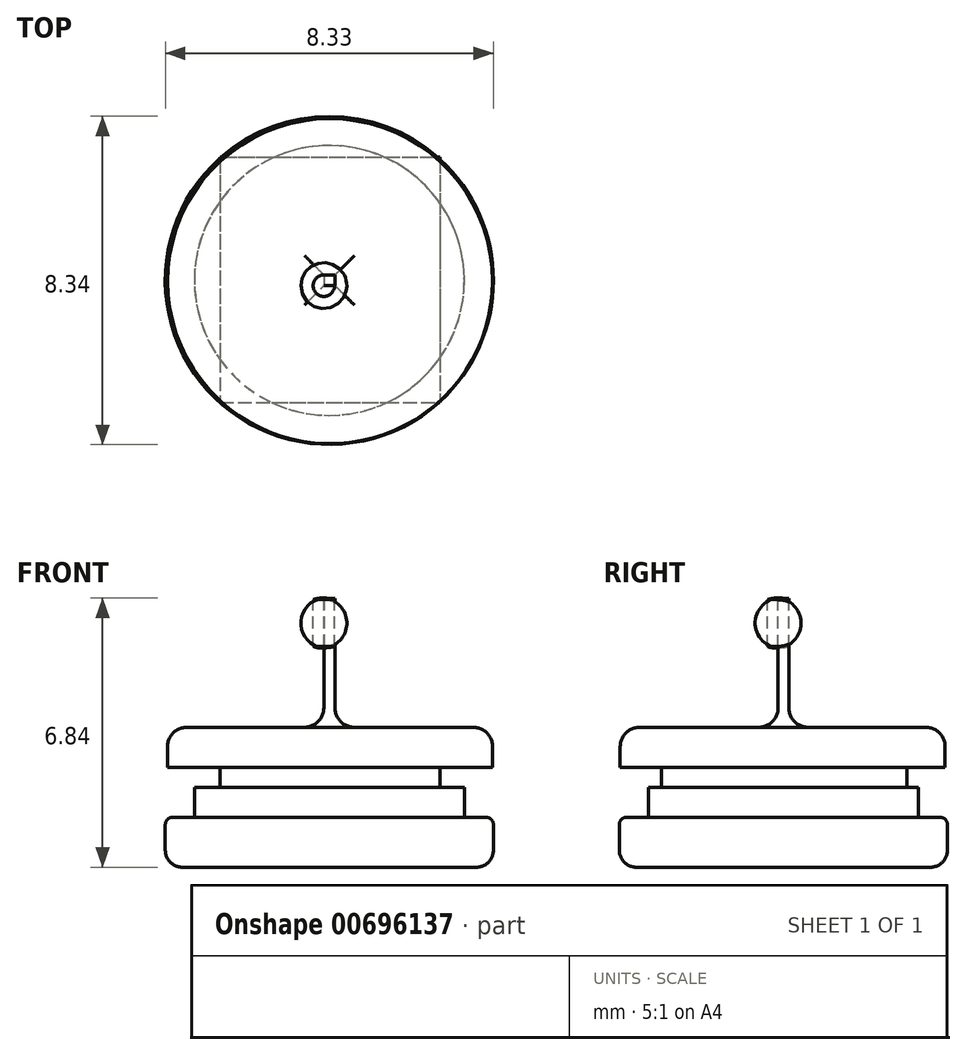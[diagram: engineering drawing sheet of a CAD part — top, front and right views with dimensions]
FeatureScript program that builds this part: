
annotation { "Feature Type Name" : "Feature", "Feature Type Description" : "" }
export const myFeature = defineFeature(function(context is Context, id is Id, definition is map)
    precondition{}
    {
        {
            var Q0;
            Q0=qCreatedBy(makeId("Top.planeOp"),FACE);
            var sketch = newSketch(context, id + "F0", { "sketchPlane" : qUnion([Q0])});
            skCircle(sketch, "E0", {"center": v(-38.02, 10.25) * mm, "radius": 4.17 * mm});
            skSolve(sketch);
        }
        {
            var Q0;
            Q0=makeQuery(id+"F0.imprint","IMPRINT",FACE,{"disambiguationData":[TD([[makeQuery(id+"F0.imprint","IMPRINT",EDGE,{"derivedFrom":sQuery(id+"F0.wireOp",EDGE,"E0")}),1.0]])]});
            var sketch = newSketch(context, id + "F1", { "sketchPlane" : qUnion([Q0])});
            skSolve(sketch);
        }
        {
            var Q0;
            Q0 = qSketchRegion(id + "F1", true);
            var Q1;
            Q1=makeQuery(id+"F0.imprint","IMPRINT",FACE,{"disambiguationData":[TD([[makeQuery(id+"F0.imprint","IMPRINT",EDGE,{"derivedFrom":sQuery(id+"F0.wireOp",EDGE,"E0")}),1.0]])]});
            extrude(context, id + "F2", {"entities" : qUnion([Q0, Q1]), "depth" : 1.27 * mm, "offsetDistance" : 25.4 * mm});
        }
        {
            var Q0;
            Q0=makeQuery(id+"F2.opExtrude","CAP_FACE",FACE,{"disambiguationData":[OSD([sQuery(id+"F0.wireOp",EDGE,"E0")])],"isStart":false});
            var sketch = newSketch(context, id + "F3", { "sketchPlane" : qUnion([Q0])});
            skCircle(sketch, "E1", {"center": v(-38.02, 10.25) * mm, "radius": 3.43 * mm});
            skSolve(sketch);
        }
        {
            var Q0;
            Q0 = qSketchRegion(id + "F3", true);
            extrude(context, id + "F4", {"entities" : qUnion([Q0]), "operationType" : NewBodyOperationType.ADD, "depth" : 0.76 * mm, "offsetDistance" : 25.4 * mm});
        }
        {
            var Q0;
            Q0=makeQuery(id+"F4.opExtrude","CAP_FACE",FACE,{"disambiguationData":[OSD([sQuery(id+"F3.wireOp",EDGE,"E1")])],"isStart":false});
            var sketch = newSketch(context, id + "F5", { "sketchPlane" : qUnion([Q0])});
            skLineSegment(sketch, "E2.bottom", {"start": v(-40.8, 13.38) * mm, "end": v(-35.2, 13.38) * mm});
            skLineSegment(sketch, "E2.top", {"start": v(-40.8, 7.15) * mm, "end": v(-35.2, 7.15) * mm});
            skLineSegment(sketch, "E2.left", {"start": v(-40.8, 13.38) * mm, "end": v(-40.8, 7.15) * mm});
            skLineSegment(sketch, "E2.right", {"start": v(-35.2, 13.38) * mm, "end": v(-35.2, 7.15) * mm});
            skSolve(sketch);
        }
        {
            var Q0;
            Q0 = qSketchRegion(id + "F5", true);
            extrude(context, id + "F6", {"entities" : qUnion([Q0]), "operationType" : NewBodyOperationType.ADD, "depth" : 0.5 * mm, "offsetDistance" : 25.4 * mm});
        }
        {
            var Q0;
            Q0=makeQuery(id+"F6.opExtrude","CAP_FACE",FACE,{"disambiguationData":[OSD([sQuery(id+"F5.wireOp",EDGE,"E2.bottom"),sQuery(id+"F5.wireOp",EDGE,"E2.top"),sQuery(id+"F5.wireOp",EDGE,"E2.left"),sQuery(id+"F5.wireOp",EDGE,"E2.right")])],"isStart":false});
            var sketch = newSketch(context, id + "F7", { "sketchPlane" : qUnion([Q0])});
            skCircle(sketch, "E3", {"center": v(-38, 10.23) * mm, "radius": 4.13 * mm});
            skPoint(sketch, "E3.centerSnap0", {"position": v(-38, 7.15) * mm});
            skSolve(sketch);
        }
        {
            var Q0;
            Q0 = qSketchRegion(id + "F7", true);
            extrude(context, id + "F8", {"entities" : qUnion([Q0]), "operationType" : NewBodyOperationType.ADD, "depth" : 1.02 * mm, "offsetDistance" : 25.4 * mm});
        }
        {
            var Q0;
            Q0=makeQuery(id+"F8.opExtrude","CAP_FACE",FACE,{"disambiguationData":[OSD([sQuery(id+"F7.wireOp",EDGE,"E3")])],"isStart":false});
            var sketch = newSketch(context, id + "F9", { "sketchPlane" : qUnion([Q0])});
            skLineSegment(sketch, "E4.bottom", {"start": v(-38.16, 10.39) * mm, "end": v(-37.87, 10.39) * mm});
            skLineSegment(sketch, "E4.top", {"start": v(-38.16, 10.12) * mm, "end": v(-37.87, 10.12) * mm});
            skLineSegment(sketch, "E4.left", {"start": v(-38.16, 10.39) * mm, "end": v(-38.16, 10.12) * mm});
            skLineSegment(sketch, "E4.right", {"start": v(-37.87, 10.39) * mm, "end": v(-37.87, 10.12) * mm});
            skSolve(sketch);
        }
        {
            var Q0;
            Q0=makeQuery(id+"F9.imprint","IMPRINT",FACE,{"disambiguationData":[TD([[makeQuery(id+"F9.imprint","IMPRINT",EDGE,{"derivedFrom":sQuery(id+"F9.wireOp",EDGE,"E4.bottom")}),-1.0]])]});
            var sketch = newSketch(context, id + "F10", { "sketchPlane" : qUnion([Q0])});
            skSolve(sketch);
        }
        {
            var Q0;
            Q0 = qSketchRegion(id + "F10", true);
            var Q1;
            Q1=makeQuery(id+"F10.imprint","IMPRINT",FACE,{"disambiguationData":[TD([[makeQuery(id+"F10.imprint","IMPRINT",EDGE,{"derivedFrom":makeQuery(id+"F9.imprint","IMPRINT",EDGE,{"derivedFrom":sQuery(id+"F9.wireOp",EDGE,"E4.bottom")})}),-1.0]])]});
            extrude(context, id + "F11", {"entities" : qUnion([Q0, Q1]), "operationType" : NewBodyOperationType.ADD, "depth" : 3.28 * mm, "offsetDistance" : 25.4 * mm});
        }
        {
            var Q0;
            Q0=makeQuery(id+"F11.opExtrude","SWEPT_FACE",FACE,{"disambiguationData":[OSD([sQuery(id+"F9.wireOp",EDGE,"E4.left")])]});
            var sketch = newSketch(context, id + "F12", { "sketchPlane" : qUnion([Q0])});
            skArc(sketch, "E5", {"start": v(-10.25, 6.83) * mm, "mid": v(-10.8, 6.14) * mm, "end": v(-10.12, 5.57) * mm});
            skSolve(sketch);
        }
        {
            var Q0;
            {var subQ0=sQuery(id+"F12.wireOp",EDGE,"E5");var subQ1=makeQuery(id+"F11.opExtrude","SWEPT_EDGE",EDGE,{"disambiguationData":[OSD([sQuery(id+"F9.wireOp",EDGE,"E4.bottom"),sQuery(id+"F9.wireOp",EDGE,"E4.left")])]});var subQ2=makeQuery(id+"F12.imprint","INTERSECT",VERTEX,{"disambiguationData":[OD(0.0)],"derivedFrom":[subQ1,subQ0]});Q0=makeQuery(id+"F12.imprint","IMPRINT",FACE,{"disambiguationData":[TD([[makeQuery(id+"F12.imprint","IMPRINT",EDGE,{"disambiguationData":[TD([[subQ2,-1.0]])],"derivedFrom":subQ0}),1.0]])]});}
            var Q1;
            Q1=makeQuery(id+"F11.opExtrude","SWEPT_EDGE",EDGE,{"disambiguationData":[OSD([sQuery(id+"F9.wireOp",EDGE,"E4.top"),sQuery(id+"F9.wireOp",EDGE,"E4.left")])]});
            revolve(context, id + "F13", {"operationType" : NewBodyOperationType.ADD, "entities" : qUnion([Q0]), "axis" : qUnion([Q1]), "revolveType" : RevolveType.FULL});
        }
        {
            var Q0;
            Q0=makeQuery(id+"F8.opExtrude","CAP_FACE",FACE,{"disambiguationData":[OSD([sQuery(id+"F7.wireOp",EDGE,"E3")])],"isStart":false});
            fillet(context, id + "F14", {"entities" : qUnion([Q0]), "radius" : 0.5 * mm, "tangentPropagation" : true, "allowEdgeOverflow" : false});
        }
        {
            var Q0;
            Q0=makeQuery(id+"F2.opExtrude","CAP_FACE",FACE,{"disambiguationData":[OSD([sQuery(id+"F0.wireOp",EDGE,"E0")])],"isStart":true});
            fillet(context, id + "F15", {"entities" : qUnion([Q0]), "radius" : 0.43 * mm, "tangentPropagation" : true, "allowEdgeOverflow" : false});
        }
        {
            var Q0;
            Q0=makeQuery(id+"F2.opExtrude","CAP_EDGE",EDGE,{"disambiguationData":[OSD([sQuery(id+"F0.wireOp",EDGE,"E0")])],"isStart":false});
            fillet(context, id + "F16", {"entities" : qUnion([Q0]), "radius" : 0.18 * mm, "tangentPropagation" : true, "allowEdgeOverflow" : false});
        }
    });
